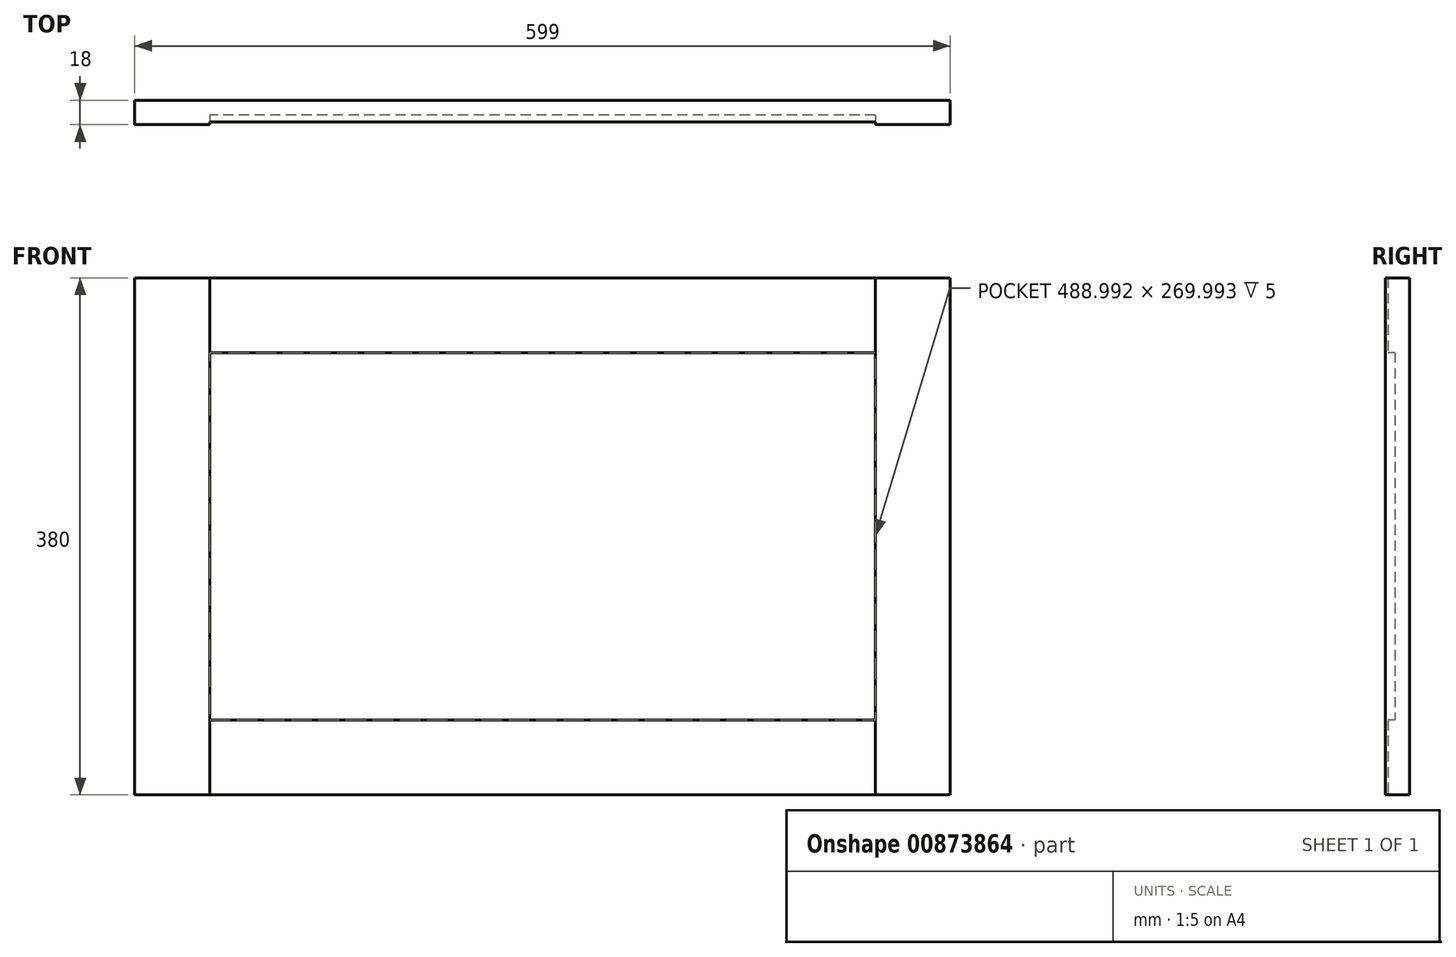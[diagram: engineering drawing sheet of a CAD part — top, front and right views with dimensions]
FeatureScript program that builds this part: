
annotation { "Feature Type Name" : "Feature", "Feature Type Description" : "" }
export const myFeature = defineFeature(function(context is Context, id is Id, definition is map)
    precondition{}
    {
        {
            var Q0;
            Q0=qCreatedBy(makeId("Front.planeOp"),FACE);
            var sketch = newSketch(context, id + "F0", { "sketchPlane" : qUnion([Q0])});
            skLineSegment(sketch, "E0.bottom", {"start": v(7.7, 0) * mm, "end": v(46.5, 0) * mm});
            skLineSegment(sketch, "E0.top", {"start": v(7.7, 45.75) * mm, "end": v(46.5, 45.75) * mm});
            skLineSegment(sketch, "E0.left", {"start": v(7.7, 0) * mm, "end": v(7.7, 45.75) * mm});
            skLineSegment(sketch, "E0.right", {"start": v(46.5, 0) * mm, "end": v(46.5, 45.75) * mm});
            skSolve(sketch);
        }
        {
            var Q0;
            Q0=makeQuery(id+"F0.imprint","IMPRINT",FACE,{"disambiguationData":[TD([[makeQuery(id+"F0.imprint","IMPRINT",EDGE,{"derivedFrom":sQuery(id+"F0.wireOp",EDGE,"E0.bottom")}),1.0]])]});
            extrude(context, id + "F1", {"entities" : qUnion([Q0]), "depth" : 18 * mm, "offsetDistance" : 25 * mm});
        }
        {
            var Q0;
            Q0=makeQuery(id+"F1.opExtrude","SWEPT_FACE",FACE,{"disambiguationData":[OSD([sQuery(id+"F0.wireOp",EDGE,"E0.left")])]});
            extrude(context, id + "F2", {"entities" : qUnion([Q0]), "operationType" : NewBodyOperationType.ADD, "oppositeDirection" : true, "depth" : 599 * mm, "offsetDistance" : 25 * mm});
        }
        {
            var Q0;
            {var subQ0=sQuery(id+"F0.wireOp",EDGE,"E0.bottom");Q0=makeQuery(id+"F2.boolean.opBoolean","MERGE",FACE,{"derivedFrom":[makeQuery(id+"F1.opExtrude","SWEPT_FACE",FACE,{"disambiguationData":[OSD([subQ0])]}),makeQuery(id+"F2.opExtrude","SWEPT_FACE",FACE,{"disambiguationData":[OSD([subQ0,sQuery(id+"F0.wireOp",EDGE,"E0.left")])]})]});}
            extrude(context, id + "F3", {"entities" : qUnion([Q0]), "operationType" : NewBodyOperationType.ADD, "oppositeDirection" : true, "depth" : 380 * mm, "offsetDistance" : 25 * mm});
        }
        {
            var Q0;
            {var subQ0=sQuery(id+"F0.wireOp",EDGE,"E0.left");var subQ1=sQuery(id+"F0.wireOp",EDGE,"E0.bottom");Q0=makeQuery(id+"F3.boolean.opBoolean","MERGE",FACE,{"derivedFrom":[makeQuery(id+"F2.boolean.opBoolean","MERGE",FACE,{"derivedFrom":[makeQuery(id+"F1.opExtrude","CAP_FACE",FACE,{"disambiguationData":[OSD([subQ1,sQuery(id+"F0.wireOp",EDGE,"E0.top"),subQ0,sQuery(id+"F0.wireOp",EDGE,"E0.right")])],"isStart":false}),makeQuery(id+"F2.opExtrude","SWEPT_FACE",FACE,{"disambiguationData":[OSD([subQ0]),TDD([makeQuery(id+"F1.opExtrude","CAP_EDGE",EDGE,{"disambiguationData":[OSD([subQ0])],"isStart":false})])]})]}),makeQuery(id+"F3.opExtrude","SWEPT_FACE",FACE,{"disambiguationData":[OSD([subQ1,subQ0]),TDD([makeQuery(id+"F2.boolean.opBoolean","MERGE",EDGE,{"derivedFrom":[makeQuery(id+"F1.opExtrude","CAP_EDGE",EDGE,{"disambiguationData":[OSD([subQ1])],"isStart":false}),makeQuery(id+"F2.opExtrude","SWEPT_EDGE",EDGE,{"disambiguationData":[OSD([subQ1,subQ0]),TDD([makeQuery(id+"F1.opExtrude","CAP_VERTEX",VERTEX,{"disambiguationData":[OSD([subQ1,subQ0])],"isStart":false})])]})]})])]})]});}
            var sketch = newSketch(context, id + "F4", { "sketchPlane" : qUnion([Q0])});
            skLineSegment(sketch, "E1", {"start": v(70.83, 380) * mm, "end": v(70.83, 0) * mm});
            skSolve(sketch);
        }
        {
            var Q0;
            {var subQ0=sQuery(id+"F4.wireOp",EDGE,"E1");Q0=makeQuery(id+"F4.imprint","IMPRINT",FACE,{"disambiguationData":[TD([[makeQuery(id+"F4.imprint","IMPRINT",EDGE,{"derivedFrom":subQ0}),-1.0]])]});}
            extrude(context, id + "F5", {"entities" : qUnion([Q0]), "operationType" : NewBodyOperationType.ADD, "depth" : 10 * mm, "offsetDistance" : 25 * mm});
        }
        {
            var Q0;
            {var subQ0=sQuery(id+"F0.wireOp",EDGE,"E0.left");var subQ1=sQuery(id+"F0.wireOp",EDGE,"E0.bottom");Q0=makeQuery(id+"F3.boolean.opBoolean","MERGE",FACE,{"derivedFrom":[makeQuery(id+"F2.boolean.opBoolean","MERGE",FACE,{"derivedFrom":[makeQuery(id+"F1.opExtrude","CAP_FACE",FACE,{"disambiguationData":[OSD([subQ1,sQuery(id+"F0.wireOp",EDGE,"E0.top"),subQ0,sQuery(id+"F0.wireOp",EDGE,"E0.right")])],"isStart":false}),makeQuery(id+"F2.opExtrude","SWEPT_FACE",FACE,{"disambiguationData":[OSD([subQ0]),TDD([makeQuery(id+"F1.opExtrude","CAP_EDGE",EDGE,{"disambiguationData":[OSD([subQ0])],"isStart":false})])]})]}),makeQuery(id+"F3.opExtrude","SWEPT_FACE",FACE,{"disambiguationData":[OSD([subQ1,subQ0]),TDD([makeQuery(id+"F2.boolean.opBoolean","MERGE",EDGE,{"derivedFrom":[makeQuery(id+"F1.opExtrude","CAP_EDGE",EDGE,{"disambiguationData":[OSD([subQ1])],"isStart":false}),makeQuery(id+"F2.opExtrude","SWEPT_EDGE",EDGE,{"disambiguationData":[OSD([subQ1,subQ0]),TDD([makeQuery(id+"F1.opExtrude","CAP_VERTEX",VERTEX,{"disambiguationData":[OSD([subQ1,subQ0])],"isStart":false})])]})]})])]})]});}
            var sketch = newSketch(context, id + "F6", { "sketchPlane" : qUnion([Q0])});
            skLineSegment(sketch, "E2", {"start": v(553.1, 380) * mm, "end": v(553.1, 0) * mm});
            skSolve(sketch);
        }
        {
            var Q0;
            {var subQ0=sQuery(id+"F6.wireOp",EDGE,"E2");Q0=makeQuery(id+"F6.imprint","IMPRINT",FACE,{"disambiguationData":[TD([[makeQuery(id+"F6.imprint","IMPRINT",EDGE,{"derivedFrom":subQ0}),1.0]])]});}
            extrude(context, id + "F7", {"entities" : qUnion([Q0]), "operationType" : NewBodyOperationType.ADD, "depth" : 10 * mm, "offsetDistance" : 25 * mm});
        }
        {
            var Q0;
            Q0=makeQuery(id+"F5.opExtrude","SWEPT_FACE",FACE,{"disambiguationData":[OSD([sQuery(id+"F4.wireOp",EDGE,"E1")])]});
            extrude(context, id + "F8", {"entities" : qUnion([Q0]), "operationType" : NewBodyOperationType.REMOVE, "oppositeDirection" : true, "depth" : 8.13 * mm, "offsetDistance" : 25 * mm});
        }
        {
            var Q0;
            Q0=makeQuery(id+"F7.opExtrude","SWEPT_FACE",FACE,{"disambiguationData":[OSD([sQuery(id+"F6.wireOp",EDGE,"E2")])]});
            extrude(context, id + "F9", {"entities" : qUnion([Q0]), "operationType" : NewBodyOperationType.ADD, "depth" : 1.41 * mm, "offsetDistance" : 25 * mm});
        }
        {
            var Q0;
            {var subQ0=sQuery(id+"F4.wireOp",EDGE,"E1");var subQ1=sQuery(id+"F0.wireOp",EDGE,"E0.left");var subQ2=sQuery(id+"F0.wireOp",EDGE,"E0.bottom");Q0=makeQuery(id+"F8.boolean.opBoolean","MERGE",FACE,{"derivedFrom":[makeQuery(id+"F3.boolean.opBoolean","MERGE",FACE,{"derivedFrom":[makeQuery(id+"F2.boolean.opBoolean","MERGE",FACE,{"derivedFrom":[makeQuery(id+"F1.opExtrude","CAP_FACE",FACE,{"disambiguationData":[OSD([subQ2,sQuery(id+"F0.wireOp",EDGE,"E0.top"),subQ1,sQuery(id+"F0.wireOp",EDGE,"E0.right")])],"isStart":false}),makeQuery(id+"F2.opExtrude","SWEPT_FACE",FACE,{"disambiguationData":[OSD([subQ1]),TDD([makeQuery(id+"F1.opExtrude","CAP_EDGE",EDGE,{"disambiguationData":[OSD([subQ1])],"isStart":false})])]})]}),makeQuery(id+"F3.opExtrude","SWEPT_FACE",FACE,{"disambiguationData":[OSD([subQ2,subQ1]),TDD([makeQuery(id+"F2.boolean.opBoolean","MERGE",EDGE,{"derivedFrom":[makeQuery(id+"F1.opExtrude","CAP_EDGE",EDGE,{"disambiguationData":[OSD([subQ2])],"isStart":false}),makeQuery(id+"F2.opExtrude","SWEPT_EDGE",EDGE,{"disambiguationData":[OSD([subQ2,subQ1]),TDD([makeQuery(id+"F1.opExtrude","CAP_VERTEX",VERTEX,{"disambiguationData":[OSD([subQ2,subQ1])],"isStart":false})])]})]})])]})]}),makeQuery(id+"F8.opExtrude","SWEPT_FACE",FACE,{"disambiguationData":[OSD([subQ0]),TDD([makeQuery(id+"F5.opExtrude","CAP_EDGE",EDGE,{"disambiguationData":[OSD([subQ0])],"isStart":true})])]})]});}
            var sketch = newSketch(context, id + "F10", { "sketchPlane" : qUnion([Q0])});
            skLineSegment(sketch, "E3", {"start": v(62.7, 339.16) * mm, "end": v(551.7, 339.16) * mm});
            skSolve(sketch);
        }
        {
            var Q0;
            {var subQ0=sQuery(id+"F10.wireOp",EDGE,"E3");Q0=makeQuery(id+"F10.imprint","IMPRINT",FACE,{"disambiguationData":[TD([[makeQuery(id+"F10.imprint","IMPRINT",EDGE,{"derivedFrom":subQ0}),1.0]])]});}
            extrude(context, id + "F11", {"entities" : qUnion([Q0]), "operationType" : NewBodyOperationType.REMOVE, "oppositeDirection" : true, "depth" : 2 * mm, "offsetDistance" : 25 * mm});
        }
        {
            var Q0;
            Q0=makeQuery(id+"F11.boolean.opBoolean","COPY",FACE,{"derivedFrom":makeQuery(id+"F11.opExtrude","SWEPT_FACE",FACE,{"disambiguationData":[OSD([sQuery(id+"F10.wireOp",EDGE,"E3")])]})});
            extrude(context, id + "F12", {"entities" : qUnion([Q0]), "operationType" : NewBodyOperationType.REMOVE, "oppositeDirection" : true, "depth" : 14.16 * mm, "offsetDistance" : 25 * mm});
        }
        {
            var Q0;
            {var subQ0=sQuery(id+"F4.wireOp",EDGE,"E1");var subQ1=sQuery(id+"F0.wireOp",EDGE,"E0.left");var subQ2=sQuery(id+"F0.wireOp",EDGE,"E0.bottom");Q0=makeQuery(id+"F8.boolean.opBoolean","MERGE",FACE,{"derivedFrom":[makeQuery(id+"F3.boolean.opBoolean","MERGE",FACE,{"derivedFrom":[makeQuery(id+"F2.boolean.opBoolean","MERGE",FACE,{"derivedFrom":[makeQuery(id+"F1.opExtrude","CAP_FACE",FACE,{"disambiguationData":[OSD([subQ2,sQuery(id+"F0.wireOp",EDGE,"E0.top"),subQ1,sQuery(id+"F0.wireOp",EDGE,"E0.right")])],"isStart":false}),makeQuery(id+"F2.opExtrude","SWEPT_FACE",FACE,{"disambiguationData":[OSD([subQ1]),TDD([makeQuery(id+"F1.opExtrude","CAP_EDGE",EDGE,{"disambiguationData":[OSD([subQ1])],"isStart":false})])]})]}),makeQuery(id+"F3.opExtrude","SWEPT_FACE",FACE,{"disambiguationData":[OSD([subQ2,subQ1]),TDD([makeQuery(id+"F2.boolean.opBoolean","MERGE",EDGE,{"derivedFrom":[makeQuery(id+"F1.opExtrude","CAP_EDGE",EDGE,{"disambiguationData":[OSD([subQ2])],"isStart":false}),makeQuery(id+"F2.opExtrude","SWEPT_EDGE",EDGE,{"disambiguationData":[OSD([subQ2,subQ1]),TDD([makeQuery(id+"F1.opExtrude","CAP_VERTEX",VERTEX,{"disambiguationData":[OSD([subQ2,subQ1])],"isStart":false})])]})]})])]})]}),makeQuery(id+"F8.opExtrude","SWEPT_FACE",FACE,{"disambiguationData":[OSD([subQ0]),TDD([makeQuery(id+"F5.opExtrude","CAP_EDGE",EDGE,{"disambiguationData":[OSD([subQ0])],"isStart":true})])]})]});}
            var sketch = newSketch(context, id + "F13", { "sketchPlane" : qUnion([Q0])});
            skLineSegment(sketch, "E4", {"start": v(551.7, 45.72) * mm, "end": v(62.7, 45.72) * mm});
            skSolve(sketch);
        }
        {
            var Q0;
            {var subQ0=sQuery(id+"F13.wireOp",EDGE,"E4");Q0=makeQuery(id+"F13.imprint","IMPRINT",FACE,{"disambiguationData":[TD([[makeQuery(id+"F13.imprint","IMPRINT",EDGE,{"derivedFrom":subQ0}),1.0]])]});}
            extrude(context, id + "F14", {"entities" : qUnion([Q0]), "operationType" : NewBodyOperationType.REMOVE, "oppositeDirection" : true, "depth" : 2 * mm, "offsetDistance" : 25 * mm});
        }
        {
            var Q0;
            Q0=makeQuery(id+"F14.boolean.opBoolean","COPY",FACE,{"derivedFrom":makeQuery(id+"F14.opExtrude","SWEPT_FACE",FACE,{"disambiguationData":[OSD([sQuery(id+"F13.wireOp",EDGE,"E4")])]})});
            extrude(context, id + "F15", {"entities" : qUnion([Q0]), "operationType" : NewBodyOperationType.REMOVE, "oppositeDirection" : true, "depth" : 9.28 * mm, "offsetDistance" : 25 * mm});
        }
        {
            var Q0;
            {var subQ0=sQuery(id+"F4.wireOp",EDGE,"E1");var subQ1=sQuery(id+"F0.wireOp",EDGE,"E0.left");var subQ2=sQuery(id+"F0.wireOp",EDGE,"E0.bottom");Q0=makeQuery(id+"F8.boolean.opBoolean","MERGE",FACE,{"derivedFrom":[makeQuery(id+"F3.boolean.opBoolean","MERGE",FACE,{"derivedFrom":[makeQuery(id+"F2.boolean.opBoolean","MERGE",FACE,{"derivedFrom":[makeQuery(id+"F1.opExtrude","CAP_FACE",FACE,{"disambiguationData":[OSD([subQ2,sQuery(id+"F0.wireOp",EDGE,"E0.top"),subQ1,sQuery(id+"F0.wireOp",EDGE,"E0.right")])],"isStart":false}),makeQuery(id+"F2.opExtrude","SWEPT_FACE",FACE,{"disambiguationData":[OSD([subQ1]),TDD([makeQuery(id+"F1.opExtrude","CAP_EDGE",EDGE,{"disambiguationData":[OSD([subQ1])],"isStart":false})])]})]}),makeQuery(id+"F3.opExtrude","SWEPT_FACE",FACE,{"disambiguationData":[OSD([subQ2,subQ1]),TDD([makeQuery(id+"F2.boolean.opBoolean","MERGE",EDGE,{"derivedFrom":[makeQuery(id+"F1.opExtrude","CAP_EDGE",EDGE,{"disambiguationData":[OSD([subQ2])],"isStart":false}),makeQuery(id+"F2.opExtrude","SWEPT_EDGE",EDGE,{"disambiguationData":[OSD([subQ2,subQ1]),TDD([makeQuery(id+"F1.opExtrude","CAP_VERTEX",VERTEX,{"disambiguationData":[OSD([subQ2,subQ1])],"isStart":false})])]})]})])]})]}),makeQuery(id+"F8.opExtrude","SWEPT_FACE",FACE,{"disambiguationData":[OSD([subQ0]),TDD([makeQuery(id+"F5.opExtrude","CAP_EDGE",EDGE,{"disambiguationData":[OSD([subQ0])],"isStart":true})])]})]});}
            extrude(context, id + "F16", {"entities" : qUnion([Q0]), "operationType" : NewBodyOperationType.REMOVE, "oppositeDirection" : true, "depth" : 7 * mm, "offsetDistance" : 25 * mm});
        }
        {
            var Q0;
            {var subQ0=sQuery(id+"F6.wireOp",EDGE,"E2");Q0=makeQuery(id+"F9.boolean.opBoolean","MERGE",FACE,{"derivedFrom":[makeQuery(id+"F7.opExtrude","CAP_FACE",FACE,{"disambiguationData":[OSD([sQuery(id+"F0.wireOp",EDGE,"E0.bottom"),sQuery(id+"F0.wireOp",EDGE,"E0.left"),subQ0])],"isStart":false}),makeQuery(id+"F9.opExtrude","SWEPT_FACE",FACE,{"disambiguationData":[OSD([subQ0]),TDD([makeQuery(id+"F7.opExtrude","CAP_EDGE",EDGE,{"disambiguationData":[OSD([subQ0])],"isStart":false})])]})]});}
            var Q1;
            Q1=makeQuery(id+"F5.opExtrude","CAP_FACE",FACE,{"disambiguationData":[OSD([sQuery(id+"F0.wireOp",EDGE,"E0.bottom"),sQuery(id+"F0.wireOp",EDGE,"E0.left"),sQuery(id+"F4.wireOp",EDGE,"E1")])],"isStart":false});
            extrude(context, id + "F17", {"entities" : qUnion([Q0, Q1]), "operationType" : NewBodyOperationType.REMOVE, "oppositeDirection" : true, "depth" : 10 * mm, "offsetDistance" : 25 * mm});
        }
    });
